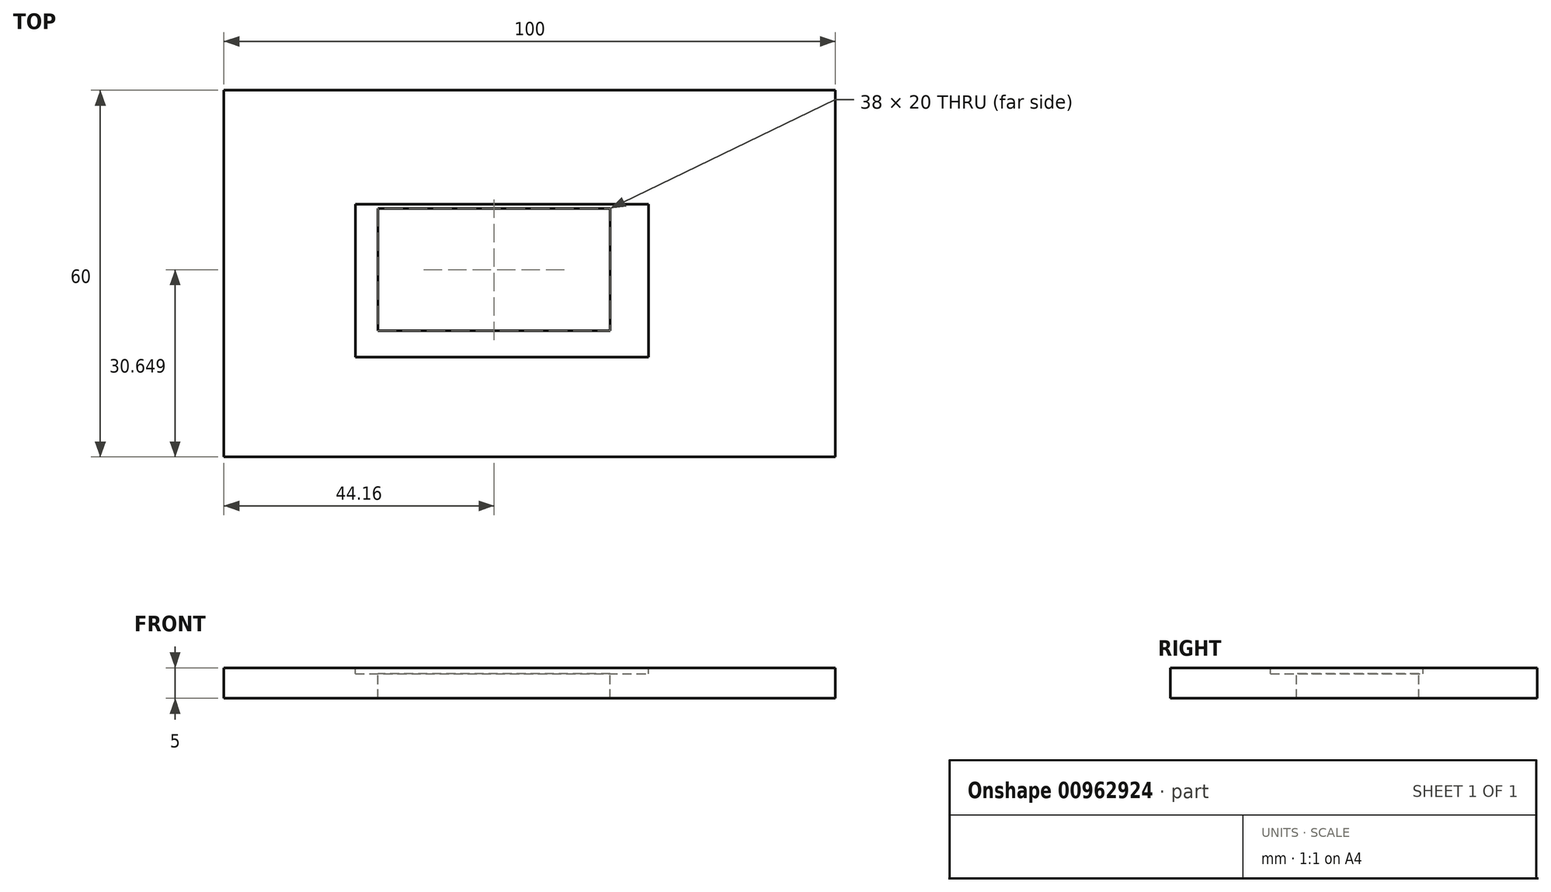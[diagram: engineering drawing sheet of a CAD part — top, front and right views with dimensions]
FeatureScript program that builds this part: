
annotation { "Feature Type Name" : "Feature", "Feature Type Description" : "" }
export const myFeature = defineFeature(function(context is Context, id is Id, definition is map)
    precondition{}
    {
        {
            var Q0;
            Q0=qCreatedBy(makeId("Top.planeOp"),FACE);
            var sketch = newSketch(context, id + "F0", { "sketchPlane" : qUnion([Q0])});
            skLineSegment(sketch, "E0.bottom", {"start": v(-44.16, -35.23) * mm, "end": v(55.84, -35.23) * mm});
            skLineSegment(sketch, "E0.top", {"start": v(-44.16, 24.77) * mm, "end": v(55.84, 24.77) * mm});
            skLineSegment(sketch, "E0.left", {"start": v(-44.16, -35.23) * mm, "end": v(-44.16, 24.77) * mm});
            skLineSegment(sketch, "E0.right", {"start": v(55.84, -35.23) * mm, "end": v(55.84, 24.77) * mm});
            skSolve(sketch);
        }
        {
            var Q0;
            Q0=qCreatedBy(makeId("Top.planeOp"),FACE);
            var sketch = newSketch(context, id + "F1", { "sketchPlane" : qUnion([Q0])});
            skLineSegment(sketch, "E1.bottom", {"start": v(-22.7, -18.89) * mm, "end": v(25.3, -18.89) * mm});
            skLineSegment(sketch, "E1.top", {"start": v(-22.7, 6.11) * mm, "end": v(25.3, 6.11) * mm});
            skLineSegment(sketch, "E1.left", {"start": v(-22.7, -18.89) * mm, "end": v(-22.7, 6.11) * mm});
            skLineSegment(sketch, "E1.right", {"start": v(25.3, -18.89) * mm, "end": v(25.3, 6.11) * mm});
            skSolve(sketch);
        }
        {
            var Q0;
            Q0=makeQuery(id+"F0.imprint","IMPRINT",FACE,{"disambiguationData":[TD([[makeQuery(id+"F0.imprint","IMPRINT",EDGE,{"derivedFrom":sQuery(id+"F0.wireOp",EDGE,"E0.bottom")}),1.0]])]});
            var sketch = newSketch(context, id + "F2", { "sketchPlane" : qUnion([Q0])});
            skLineSegment(sketch, "E2.bottom", {"start": v(19, 5.42) * mm, "end": v(-19, 5.42) * mm});
            skLineSegment(sketch, "E2.top", {"start": v(19, -14.58) * mm, "end": v(-19, -14.58) * mm});
            skLineSegment(sketch, "E2.left", {"start": v(19, 5.42) * mm, "end": v(19, -14.58) * mm});
            skLineSegment(sketch, "E2.right", {"start": v(-19, 5.42) * mm, "end": v(-19, -14.58) * mm});
            skPoint(sketch, "E2.middle", {"position": v(0, -4.58) * mm});
            skSolve(sketch);
        }
        {
            var Q0;
            Q0 = qSketchRegion(id + "F0", true);
            extrude(context, id + "F3", {"entities" : qUnion([Q0]), "oppositeDirection" : true, "depth" : 5 * mm, "offsetDistance" : 25 * mm});
        }
        {
            var Q0;
            Q0 = qSketchRegion(id + "F1", true);
            extrude(context, id + "F4", {"entities" : qUnion([Q0]), "operationType" : NewBodyOperationType.REMOVE, "oppositeDirection" : true, "depth" : 1 * mm, "offsetDistance" : 25 * mm});
        }
        {
            var Q0;
            Q0 = qSketchRegion(id + "F2", true);
            extrude(context, id + "F5", {"entities" : qUnion([Q0]), "operationType" : NewBodyOperationType.REMOVE, "oppositeDirection" : true, "depth" : 10 * mm, "offsetDistance" : 25 * mm});
        }
    });
